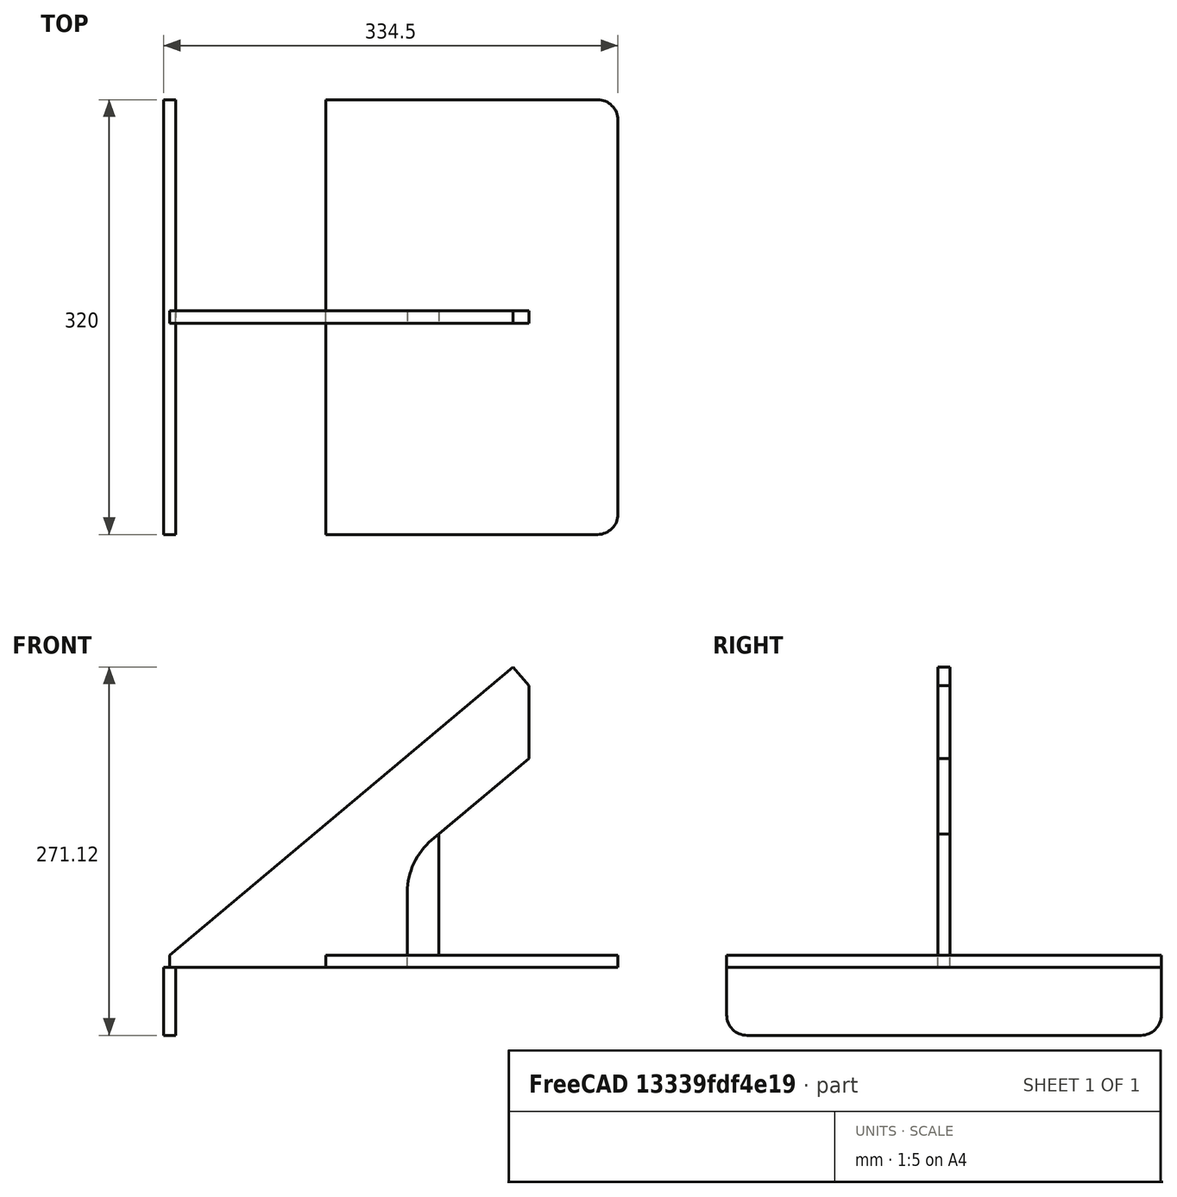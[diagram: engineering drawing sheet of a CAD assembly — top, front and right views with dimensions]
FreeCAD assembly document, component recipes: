
FREECAD ASSEMBLY — COMPONENT RECIPES ("Wing_Assembly_right")

This assembly document has 4 components, labeled P0..P3 below (a component is one placed body or linked part). 4 of them carry a construction recipe — the FreeCAD feature program that regenerates the part from scratch, quoted from this document or its linked companion documents; the rest are supplied as boundary geometry only. No exploded tour is included for this assembly.
COMPONENT P0 — recipe-attached ("Rib", modeled in this document).
Construction recipe (the document's own serialized feature program — sketch geometry with constraints, then the solid features built on it; lengths are millimeters unless a unit is written):

FEATURE [PartDesign::CoordinateSystem] LCS_0003
  AttacherType = Attacher::AttachEngine3D
  MapMode = 2
  Support = -> [X_Axis004]
FEATURE [Sketcher::SketchObject] Sketch003
  FullyConstrained = true
  MapMode = 5
  Placement = pos=(0,0,0) rot=(0.57735,0.57735,0.57735;2.0944rad)
  Support = -> [YZ_Plane004]
  expr: Constraints[13] = <<key_dimensions>>#<<Dimensions>>.wing_depth
  expr: Constraints[19] = <<key_dimensions>>#<<Dimensions>>.cradle_rounded
  expr: Constraints[24] = <<key_dimensions>>#<<Dimensions>>.MDF_thick
  sketch-geometry (9):
    g0: LineSegment StartX=-160 StartY=-9 StartZ=0 EndX=160 EndY=-9 EndZ=0
    g1: LineSegment StartX=160 StartY=-9 StartZ=0 EndX=160 EndY=-44 EndZ=0
    g2: LineSegment StartX=145 StartY=-59 StartZ=0 EndX=-145 EndY=-59 EndZ=0
    g3: LineSegment StartX=-160 StartY=-44 StartZ=0 EndX=-160 EndY=-9 EndZ=0
    g4: LineSegment StartX=145 StartY=-9 StartZ=0 EndX=145 EndY=-59 EndZ=0
    g5: LineSegment StartX=-160 StartY=-44 StartZ=0 EndX=160 EndY=-44 EndZ=0
    g6: ArcOfCircle CenterX=-145 CenterY=-44 CenterZ=0 NormalX=0 NormalY=0 NormalZ=1 AngleXU=0 Radius=15 StartAngle=3.14159 EndAngle=4.71239
    g7: ArcOfCircle CenterX=145 CenterY=-44 CenterZ=0 NormalX=0 NormalY=0 NormalZ=1 AngleXU=0 Radius=15 StartAngle=4.71239 EndAngle=6.28319
    g8: GeomPoint X=0 Y=-9 Z=0
  constraints (25):
    c: Coincident(g0,g1)
    c: Coincident(g3,g0)
    c: Horizontal(g0)
    c: Horizontal(g2)
    c: Vertical(g1)
    c: Vertical(g3)
    c: PointOnObject(g4,g0)
    c: PointOnObject(g4,g2)
    c: Vertical(g4)
    c: PointOnObject(g5,g3)
    c: PointOnObject(g5,g1)
    c: Horizontal(g5)
    c: DistanceY(g4,g4) = 50
    c: DistanceX(g5,g5) = 320
    c: Tangent(g3,g6) = 1.5708
    c: Tangent(g2,g6) = 1.5708
    c: Tangent(g1,g7) = 1.5708
    c: Tangent(g2,g7) = 1.5708
    c: Equal(g7,g6)
    c: Radius(g7) = 15
    c: PointOnObject(g1,g5)
    c: PointOnObject(g2,g4)
    c: PointOnObject(g8,g-2)
    c: Symmetric(g0,g0,g8)
    c: DistanceY(g8,g-1) = 9
FEATURE [PartDesign::Pad] Pad003
  Direction = (1,1,1)
  Length = 9
  Length2 = 100
  Midplane = true
  Placement = pos=(0,0,0) rot=(0.57735,0.57735,0.57735;2.0944rad)
  Profile = -> Sketch003
  Type = 0
  expr: Length = <<key_dimensions>>#<<Dimensions>>.MDF_thick
FEATURE [PartDesign::Body] Rib
  Group = -> [LCS_0003,Sketch003,Pad003]
  Origin = -> Origin004
  Tip = -> Pad003
COMPONENT P1 — recipe-attached ("Wing", modeled in this document).
Construction recipe (the document's own serialized feature program — sketch geometry with constraints, then the solid features built on it; lengths are millimeters unless a unit is written):

FEATURE [PartDesign::CoordinateSystem] LCS_0002
  AttacherType = Attacher::AttachEngine3D
  MapMode = 2
  Support = -> [X_Axis003]
FEATURE [Sketcher::SketchObject] Sketch002
  FullyConstrained = true
  MapMode = 5
  Support = -> [XY_Plane003]
  expr: Constraints[11] = <<key_dimensions>>#<<Dimensions>>.wing_depth
  expr: Constraints[15] = <<key_dimensions>>#<<Dimensions>>.wing_length
  expr: Constraints[16] = <<key_dimensions>>#<<Dimensions>>.acrylic_width
  expr: Constraints[22] = <<key_dimensions>>#<<Dimensions>>.cradle_rounded
  sketch-geometry (9):
    g0: LineSegment StartX=115 StartY=160 StartZ=0 EndX=315 EndY=160 EndZ=0
    g1: LineSegment StartX=330 StartY=145 StartZ=0 EndX=330 EndY=-145 EndZ=0
    g2: LineSegment StartX=315 StartY=-160 StartZ=0 EndX=115 EndY=-160 EndZ=0
    g3: LineSegment StartX=115 StartY=-160 StartZ=0 EndX=115 EndY=160 EndZ=0
    g4: GeomPoint X=115 Y=0 Z=0
    g5: LineSegment StartX=315 StartY=160 StartZ=0 EndX=315 EndY=-160 EndZ=0
    g6: LineSegment StartX=115 StartY=145 StartZ=0 EndX=330 EndY=145 EndZ=0
    g7: ArcOfCircle CenterX=315 CenterY=145 CenterZ=0 NormalX=0 NormalY=0 NormalZ=1 AngleXU=0 Radius=15 StartAngle=4e-16 EndAngle=1.5708
    g8: ArcOfCircle CenterX=315 CenterY=-145 CenterZ=0 NormalX=0 NormalY=0 NormalZ=1 AngleXU=0 Radius=15 StartAngle=4.71239 EndAngle=6.28319
  constraints (25):
    c: Coincident(g2,g3)
    c: Coincident(g3,g0)
    c: Horizontal(g0)
    c: Horizontal(g2)
    c: Vertical(g1)
    c: Vertical(g3)
    c: PointOnObject(g4,g-1)
    c: Symmetric(g2,g0,g4)
    c: PointOnObject(g5,g0)
    c: PointOnObject(g5,g2)
    c: Vertical(g5)
    c: DistanceY(g5,g5) = 320
    c: PointOnObject(g6,g3)
    c: PointOnObject(g6,g1)
    c: Horizontal(g6)
    c: DistanceX(g6,g6) = 215
    c: DistanceX(g-1,g6) = 330
    c: Tangent(g0,g7) = 1.5708
    c: Tangent(g1,g7) = 1.5708
    c: Tangent(g2,g8) = 1.5708
    c: Tangent(g1,g8) = 1.5708
    c: Equal(g8,g7)
    c: Radius(g7) = 15
    c: PointOnObject(g1,g6)
    c: PointOnObject(g0,g5)
FEATURE [PartDesign::Pad] Pad002
  Direction = (1,1,1)
  Length = 9
  Length2 = 100
  Profile = -> Sketch002
  Reversed = true
  Type = 0
  expr: Length = <<key_dimensions>>#<<Dimensions>>.MDF_thick
FEATURE [PartDesign::Body] Wing
  Group = -> [LCS_0002,Sketch002,Pad002]
  Origin = -> Origin003
  Tip = -> Pad002
COMPONENT P2 — recipe-attached ("Wing_Support_B", modeled in this document).
Construction recipe (the document's own serialized feature program — sketch geometry with constraints, then the solid features built on it; lengths are millimeters unless a unit is written):

FEATURE [PartDesign::CoordinateSystem] LCS_0001
  AttacherType = Attacher::AttachEngine3D
  MapMode = 2
  Support = -> [X_Axis002]
FEATURE [Sketcher::SketchObject] Sketch001  label="Wing_Support_B_Sketch"
  FullyConstrained = true
  MapMode = 5
  Placement = pos=(0,0,0) rot=(1,0,0;1.5708rad)
  Support = -> [XZ_Plane002]
  expr: Constraints[11] = <<key_dimensions>>#<<Dimensions>>.acrylic_width
  expr: Constraints[17] = <<key_dimensions>>#<<Dimensions>>.MDF_thick * 2
  expr: Constraints[16] = <<key_dimensions>>#<<Dimensions>>.MDF_thick
  expr: Constraints[7] = <<key_dimensions>>#<<Dimensions>>.cradle_tilting
  sketch-geometry (9):
    g0: LineSegment StartX=0 StartY=-9 StartZ=0 EndX=0 EndY=0 EndZ=0
    g1: LineSegment StartX=0 StartY=0 StartZ=0 EndX=252.795 EndY=212.12 EndZ=0
    g2: LineSegment StartX=252.795 StartY=212.12 StartZ=0 EndX=264.365 EndY=198.331 EndZ=0
    g3: LineSegment StartX=264.365 StartY=198.331 StartZ=0 EndX=264.365 EndY=144.809 EndZ=0
    g4: LineSegment StartX=264.365 StartY=144.809 StartZ=0 EndX=192.861 EndY=84.8102 EndZ=0
    g5: LineSegment StartX=175 StartY=-9 StartZ=0 EndX=0 EndY=-9 EndZ=0
    g6: LineSegment StartX=154.936 StartY=130.007 StartZ=0 EndX=192.861 EndY=84.8102 EndZ=0
    g7: LineSegment StartX=175 StartY=-9 StartZ=0 EndX=175 EndY=46.508 EndZ=0
    g8: ArcOfCircle CenterX=225 CenterY=46.508 CenterZ=0 NormalX=0 NormalY=0 NormalZ=1 AngleXU=0 Radius=50 StartAngle=2.26893 EndAngle=3.14159
  constraints (26):
    c: Coincident(g0,g1)
    c: Coincident(g1,g2)
    c: Coincident(g2,g3)
    c: Vertical(g3)
    c: Coincident(g3,g4)
    c: Coincident(g5,g0)
    c: Horizontal(g5)
    c: Angle(g1) = 0.698132
    c: Perpendicular(g1,g2)
    c: Parallel(g4,g1)
    c: Vertical(g0)
    c: Distance(g1) = 330
    c: PointOnObject(g6,g1)
    c: PointOnObject(g6,g4)
    c: Perpendicular(g1,g6)
    c: Distance(g6) = 59
    c: DistanceY(g0,g0) = 9
    c: Distance(g2) = 18
    c: Coincident(g0,g-1)
    c: PointOnObject(g4,g6)
    c: Coincident(g5,g7)
    c: DistanceX(g5,g5) = 175
    c: Vertical(g7)
    c: Tangent(g8,g4) = -1.5708
    c: Tangent(g8,g7) = 1.5708
    c: Radius(g8) = 50
FEATURE [PartDesign::Pad] Pad001
  Direction = (1,1,1)
  Length = 9
  Length2 = 100
  Midplane = true
  Placement = pos=(0,0,0) rot=(1,0,0;1.5708rad)
  Profile = -> Sketch001
  Type = 0
  expr: Length = <<key_dimensions>>#<<Dimensions>>.MDF_thick
FEATURE [PartDesign::Body] Wing_Support_B
  Group = -> [LCS_0001,Sketch001,Pad001]
  Origin = -> Origin002
  Tip = -> Pad001
COMPONENT P3 — recipe-attached ("Wing_support_A", modeled in this document).
Construction recipe (the document's own serialized feature program — sketch geometry with constraints, then the solid features built on it; lengths are millimeters unless a unit is written):

FEATURE [PartDesign::CoordinateSystem] LCS_0
  AttacherType = Attacher::AttachEngine3D
  MapMode = 2
  Support = -> [X_Axis001]
FEATURE [Sketcher::SketchObject] Sketch  label="Wing_Support_A_Sketch"
  FullyConstrained = true
  MapMode = 5
  Placement = pos=(0,0,0) rot=(1,0,0;1.5708rad)
  Support = -> [XZ_Plane001]
  expr: Constraints[13] = <<key_dimensions>>#<<Dimensions>>.acrylic_width
  expr: Constraints[19] = <<key_dimensions>>#<<Dimensions>>.MDF_thick * 2
  expr: Constraints[18] = <<key_dimensions>>#<<Dimensions>>.MDF_thick
  expr: Constraints[9] = <<key_dimensions>>#<<Dimensions>>.cradle_tilting
  sketch-geometry (10):
    g0: LineSegment StartX=0 StartY=-9 StartZ=0 EndX=0 EndY=0 EndZ=0
    g1: LineSegment StartX=0 StartY=0 StartZ=0 EndX=252.795 EndY=212.12 EndZ=0
    g2: LineSegment StartX=252.795 StartY=212.12 StartZ=0 EndX=264.365 EndY=198.331 EndZ=0
    g3: LineSegment StartX=264.365 StartY=198.331 StartZ=0 EndX=264.365 EndY=144.809 EndZ=0
    g4: LineSegment StartX=264.365 StartY=144.809 StartZ=0 EndX=198 EndY=89.1227 EndZ=0
    g5: LineSegment StartX=198 StartY=89.1227 StartZ=0 EndX=198 EndY=0 EndZ=0
    g6: LineSegment StartX=175 StartY=-9 StartZ=0 EndX=0 EndY=-9 EndZ=0
    g7: LineSegment StartX=160.076 StartY=134.319 StartZ=0 EndX=198 EndY=89.1227 EndZ=0
    g8: LineSegment StartX=175 StartY=-9 StartZ=0 EndX=175 EndY=0 EndZ=0
    g9: LineSegment StartX=175 StartY=0 StartZ=0 EndX=198 EndY=0 EndZ=0
  constraints (30):
    c: Coincident(g0,g1)
    c: Coincident(g1,g2)
    c: Coincident(g2,g3)
    c: Vertical(g3)
    c: Coincident(g3,g4)
    c: Coincident(g4,g5)
    c: Vertical(g5)
    c: Coincident(g6,g0)
    c: Horizontal(g6)
    c: Angle(g1) = 0.698132
    c: Perpendicular(g1,g2)
    c: Parallel(g4,g1)
    c: Vertical(g0)
    c: Distance(g1) = 330
    c: PointOnObject(g7,g1)
    c: PointOnObject(g7,g4)
    c: Perpendicular(g1,g7)
    c: Distance(g7) = 59
    c: DistanceY(g0,g0) = 9
    c: Distance(g2) = 18
    c: Coincident(g0,g-1)
    c: PointOnObject(g4,g7)
    c: Coincident(g8,g9)
    c: Horizontal(g9)
    c: Coincident(g6,g8)
    c: Coincident(g5,g9)
    c: PointOnObject(g0,g9)
    c: DistanceX(g6,g6) = 175
    c: Vertical(g8)
    c: DistanceX(g8,g4) = 23
FEATURE [PartDesign::Pad] Pad
  Direction = (1,1,1)
  Length = 9
  Length2 = 100
  Midplane = true
  Placement = pos=(0,0,0) rot=(1,0,0;1.5708rad)
  Profile = -> Sketch
  Type = 0
  expr: Length = <<key_dimensions>>#<<Dimensions>>.MDF_thick
FEATURE [PartDesign::Body] Wing_support_A
  Group = -> [LCS_0,Sketch,Pad]
  Origin = -> Origin001
  Tip = -> Pad
PROVENANCE & LICENSES
A FreeCAD (.FCStd) document from a public repository crawl; recipes are the document's own serialized feature recipes (and, for linked parts, companion documents' recipes).
License: cc-by-sa-4.0.
